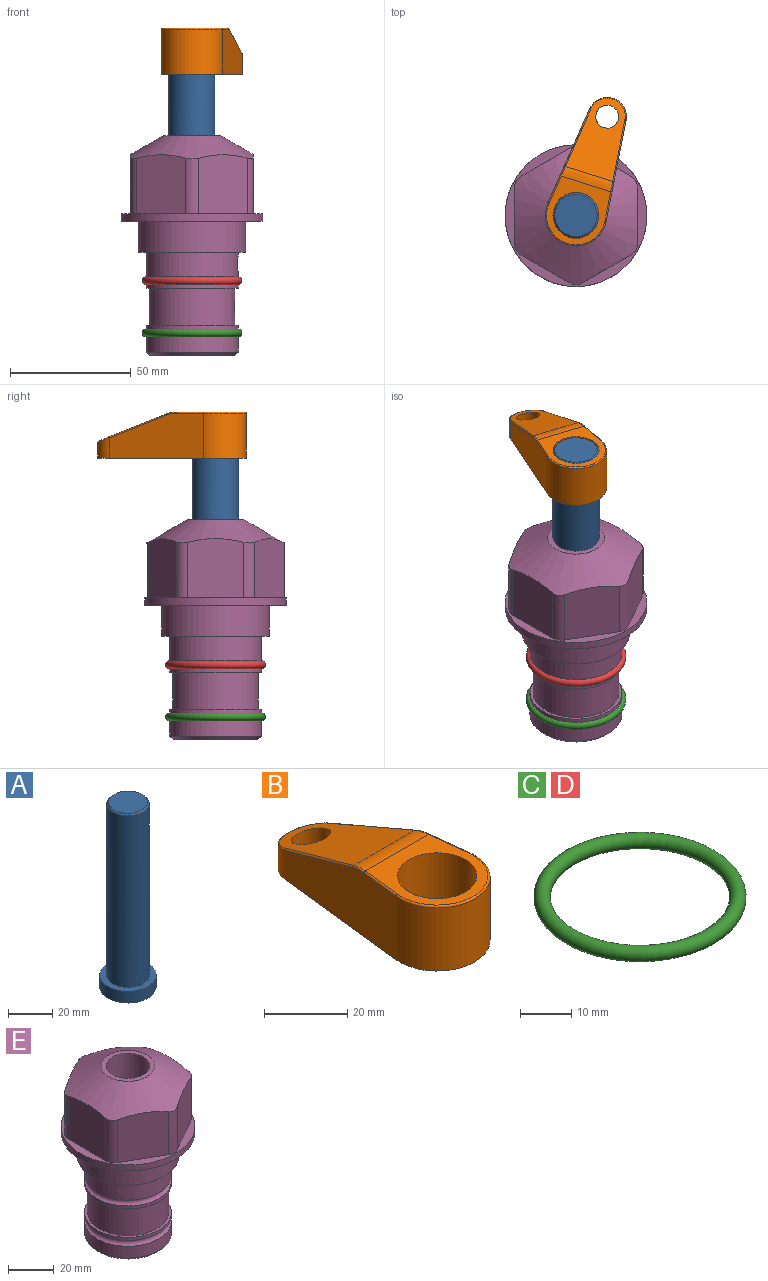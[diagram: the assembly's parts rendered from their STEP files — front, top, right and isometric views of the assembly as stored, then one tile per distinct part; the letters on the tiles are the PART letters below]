
ASSEMBLY  parts=5 mates=3
PART A: 6 faces, bbox 25.4x25.4x101.6 mm
  f0: plane 17.46x17.46mm, normal (0,0,1), area 239.5mm2, adj f5
  f1: plane 25.4x25.4mm, normal (0,0,-1), area 506.7mm2, adj f2
  f2: cylinder r=12.7mm len=25.4mm, axis (0,0,1), area 506.7mm2, adj f1,f3
  f3: plane 25.4x25.4mm, normal (0,0,1), area 221.7mm2, adj f2,f4
  f4: cylinder r=9.53mm len=94.46mm, axis (0,0,1), area 5653mm2, adj f3,f5
  f5: cone r=8.73mm half-angle=45deg, axis (0,0,-1), area 64.4mm2, adj f0,f4
PART B: 44 faces, bbox 27.5x64.5x19.1 mm
  f0: plane 2.3x0.95mm, normal (0,0,-1), area 1mm2, adj f25,f30,f34
  f1: plane 63.5x25.4mm, normal (0,0,-1), area 561.7mm2, adj f2,f3,f4,f5,f6,f7,f19,f20
  f2: cylinder r=12.7mm len=25.4mm, axis (0,0,-1), area 792.2mm2, adj f1,f3,f5,f13
  f3: plane 42.33x18.54mm, normal (0.99,0.11,0), area 647mm2, adj f1,f2,f4,f11,f12,f14
  f4: cylinder r=7.94mm len=15.78mm, axis (0,0,-1), area 158.6mm2, adj f1,f3,f5,f16
  f5: plane 42.33x18.54mm, normal (-0.99,0.11,0), area 647mm2, adj f1,f2,f4,f15,f17,f18
  f6: cylinder r=9.53mm len=19.05mm, axis (0,0,-1), area 1140.1mm2, adj f1,f8
  f7: cylinder r=4.76mm len=10.98mm, axis (0,0,-1), area 276.1mm2, adj f1,f9
  f8: plane 25.83x24.38mm, normal (0,0,1), area 262.2mm2, adj f6,f10,f11,f13,f15
  f9: plane 32.49x20.55mm, normal (0,0.34,0.94), area 489.9mm2, adj f7,f10,f14,f16,f18
  f10: cylinder r=12.7mm len=21.49mm, axis (-1,0,0), area 93.2mm2, adj f8,f9,f12,f17
  f11: cylinder r=0.51mm len=12.34mm, axis (0.11,-0.99,0), area 9.9mm2, adj f3,f8,f12,f13
  f12: bspline ~7.62x1.64mm, area 3.5mm2, adj f3,f10,f11,f14
  f13: torus R=12.19mm, axis (0,0,1), area 33.6mm2, adj f2,f8,f11,f15
  f14: cylinder r=0.51mm len=26.01mm, axis (0.1,-0.93,0.34), area 21.6mm2, adj f3,f9,f12,f16
  f15: cylinder r=0.51mm len=12.34mm, axis (0.11,0.99,0), area 9.9mm2, adj f5,f8,f13,f17
  f16: bspline ~15.78x7.05mm, area 15.7mm2, adj f4,f9,f14,f18
  f17: bspline ~7.62x1.64mm, area 3.5mm2, adj f5,f10,f15,f18
  f18: cylinder r=0.51mm len=26.01mm, axis (0.1,0.93,-0.34), area 21.6mm2, adj f5,f9,f16,f17
  f19: plane 21.6x14.29mm, normal (-0.99,-0.11,0), area 242.6mm2, adj f1,f26,f28,f34,f36,f38
  f20: plane 21.6x14.29mm, normal (0.99,-0.11,0), area 242.6mm2, adj f1,f27,f29,f37,f39,f41
  f21: cylinder r=12.7mm len=14.29mm, axis (0,0,-1), area 173.2mm2, adj f1,f26,f27,f30,f31,f33
  f22: cylinder r=7.94mm len=7.63mm, axis (0,0,-1), area 53.8mm2, adj f1,f28,f29,f42
  f23: plane 2.3x0.95mm, normal (0,0,-1), area 1mm2, adj f25,f33,f37
  f24: plane 17.94x12.32mm, normal (0,-0.34,-0.94), area 191.2mm2, adj f25,f38,f41,f42
  f25: cylinder r=9.53mm len=12.93mm, axis (-1,0,0), area 37.5mm2, adj f0,f23,f24,f31,f36,f39
  f26: cylinder r=1.59mm len=14.29mm, axis (0,0,-1), area 49mm2, adj f1,f19,f21,f32
  f27: cylinder r=1.59mm len=14.29mm, axis (0,0,-1), area 49mm2, adj f1,f20,f21,f35
  f28: cylinder r=1.59mm len=7.28mm, axis (0,0,-1), area 22.1mm2, adj f1,f19,f22,f40
  f29: cylinder r=1.59mm len=7.28mm, axis (0,0,-1), area 22.1mm2, adj f1,f20,f22,f43
  f30: torus R=14.29mm, axis (0,0,1), area 5.8mm2, adj f0,f21,f31,f32
  f31: bspline ~11.06x2.73mm, area 20.8mm2, adj f21,f25,f30,f33
  f32: sphere r=1.59mm, area 5.4mm2, adj f26,f30,f34
  f33: torus R=14.29mm, axis (0,0,1), area 5.8mm2, adj f21,f23,f31,f35
  f34: cylinder r=1.59mm len=1.68mm, axis (-0.11,0.99,0), area 2.4mm2, adj f0,f19,f32,f36
  f35: sphere r=1.59mm, area 5.4mm2, adj f27,f33,f37
  f36: bspline ~5.82x2.33mm, area 7.7mm2, adj f19,f25,f34,f38
  f37: cylinder r=1.59mm len=1.68mm, axis (0.11,0.99,0), area 2.4mm2, adj f20,f23,f35,f39
  f38: cylinder r=1.59mm len=18.33mm, axis (0.1,-0.93,0.34), area 46.7mm2, adj f19,f24,f36,f40
  f39: bspline ~5.82x2.33mm, area 7.7mm2, adj f20,f25,f37,f41
  f40: sphere r=1.59mm, area 3.6mm2, adj f28,f38,f42
  f41: cylinder r=1.59mm len=18.33mm, axis (0.1,0.93,-0.34), area 46.7mm2, adj f20,f24,f39,f43
  f42: bspline ~8.31x1.84mm, area 15.3mm2, adj f22,f24,f40,f43
  f43: sphere r=1.59mm, area 3.6mm2, adj f29,f41,f42
PART C: 1 faces, bbox 44.7x44.7x3.2 mm
  f0: torus R=19.05mm, axis (0,0,1), area 1193.9mm2
PART D: same geometry as C
PART E: 36 faces, bbox 58.7x58.7x91.2 mm
  f0: cylinder r=17.78mm len=35.56mm, axis (0,0,1), area 1670.8mm2, adj f23,f24,f31
  f1: cylinder r=19.05mm len=38.1mm, axis (0,0,1), area 1191.9mm2, adj f26,f27,f30
  f2: plane 58.66x58.66mm, normal (0,0,-1), area 1150.6mm2, adj f3,f28
  f3: cylinder r=29.33mm len=58.66mm, axis (0,0,-1), area 585.1mm2, adj f2,f4
  f4: plane 58.66x58.66mm, normal (0,0,1), area 475.9mm2, adj f3,f5,f6,f7,f8,f9,f10,f11
  f5: plane 24.5x20.32mm, normal (-0.5,0.87,0), area 562.8mm2, adj f4,f15,f16,f17
  f6: plane 24.5x20.32mm, normal (0.5,0.87,0), area 562.8mm2, adj f4,f14,f15,f17
  f7: plane 24.5x23.48mm, normal (1,0,0), area 562.8mm2, adj f4,f13,f14,f17
  f8: plane 24.5x20.32mm, normal (0.5,-0.87,0), area 562.8mm2, adj f4,f12,f13,f17
  f9: plane 24.5x20.32mm, normal (-0.5,-0.87,0), area 562.8mm2, adj f4,f11,f12,f17
  f10: plane 24.5x23.48mm, normal (-1,0,0), area 562.8mm2, adj f4,f11,f16,f17
  f11: cylinder r=5.08mm len=23.01mm, axis (0,0,-1), area 121.2mm2, adj f4,f9,f10,f17
  f12: cylinder r=5.08mm len=23.01mm, axis (0,0,-1), area 121.2mm2, adj f4,f8,f9,f17
  f13: cylinder r=5.08mm len=23.01mm, axis (0,0,-1), area 121.2mm2, adj f4,f7,f8,f17
  f14: cylinder r=5.08mm len=23.01mm, axis (0,0,-1), area 121.2mm2, adj f4,f6,f7,f17
  f15: cylinder r=5.08mm len=23.01mm, axis (0,0,-1), area 121.2mm2, adj f4,f5,f6,f17
  f16: cylinder r=5.08mm len=23.01mm, axis (0,0,-1), area 121.2mm2, adj f4,f5,f10,f17
  f17: cone r=11.73mm half-angle=60deg, axis (0,0,-1), area 2071.8mm2, adj f5,f6,f7,f8,f9,f10,f11,f12
  f18: plane 23.46x23.46mm, normal (0,0,1), area 147.4mm2, adj f17,f35
  f19: plane 34.93x34.93mm, normal (0,0,-1), area 958mm2, adj f29
  f20: cylinder r=19.05mm len=38.1mm, axis (0,0,1), area 760.1mm2, adj f21,f29
  f21: torus R=19.05mm, axis (0,0,1), area 565.3mm2, adj f20,f22
  f22: cylinder r=19.05mm len=38.1mm, axis (0,0,1), area 190mm2, adj f21,f23
  f23: plane 38.1x38.1mm, normal (0,0,1), area 146.9mm2, adj f0,f22
  f24: plane 38.1x38.1mm, normal (0,0,-1), area 146.9mm2, adj f0,f25
  f25: cylinder r=19.05mm len=38.1mm, axis (0,0,1), area 190mm2, adj f24,f26
  f26: torus R=19.05mm, axis (0,0,1), area 565.3mm2, adj f1,f25
  f27: plane 44.45x44.45mm, normal (0,0,-1), area 411.7mm2, adj f1,f28
  f28: cylinder r=22.23mm len=44.45mm, axis (0,0,1), area 1773.5mm2, adj f2,f27
  f29: cone r=19.05mm half-angle=45deg, axis (0,0,1), area 257.5mm2, adj f19,f20
  f30: cylinder r=3.17mm len=6.75mm, axis (-1,0,0), area 128mm2, adj f1,f33
  f31: cylinder r=3.17mm len=6.35mm, axis (-1,0,0), area 102.5mm2, adj f0,f33
  f32: plane 25.4x25.4mm, normal (0,0,1), area 506.7mm2, adj f33
  f33: cylinder r=12.7mm len=66.42mm, axis (0,0,-1), area 5236.2mm2, adj f30,f31,f32,f34
  f34: cone r=9.53mm half-angle=30deg, axis (0,0,-1), area 443.4mm2, adj f33,f35
  f35: cylinder r=9.53mm len=19.05mm, axis (0,0,-1), area 849mm2, adj f18,f34
PLACE A rot(axis=(0,0,1),72.4deg) t=(0,0,6.38)mm
PLACE B rot(axis=(0,0,-1),17.6deg) t=(0,0,60.99)mm
PLACE C t=(0,0,-21.59)mm
PLACE D at identity
PLACE E at identity fixed
MATE fastened C.f0 <-> E.f0  axis (0,0,1) through (0,0,-46.1)mm
MATE cylindrical A.f2 <-> E.f0  axis (0,0,1) through (0,0,32.01)mm
MATE fastened B.f2 <-> A.f2  axis (0,0,1) through (0,0,80.04)mm
